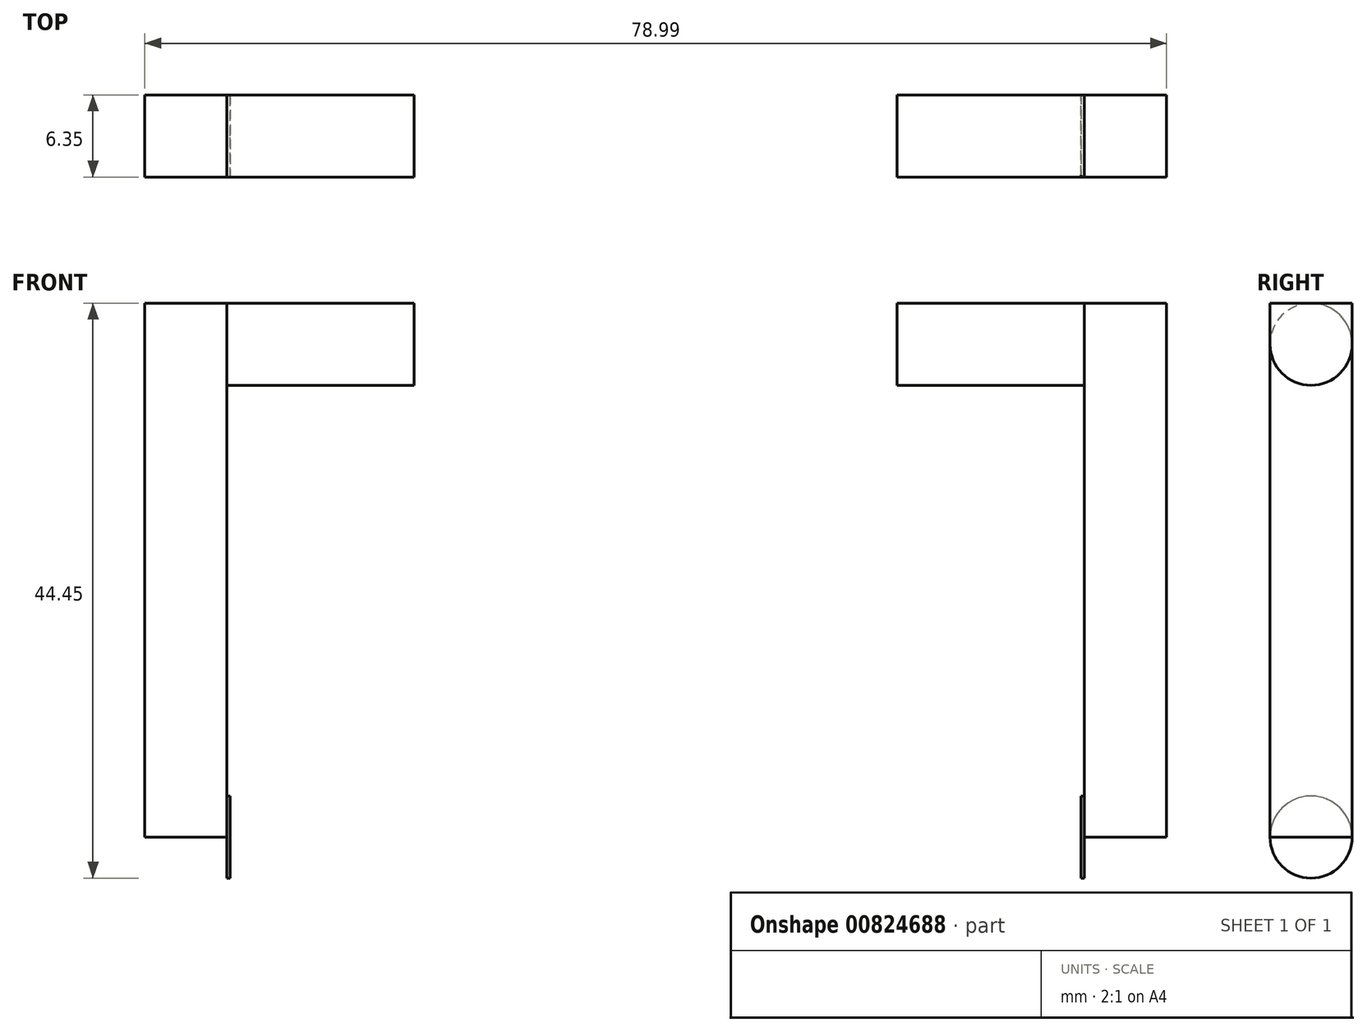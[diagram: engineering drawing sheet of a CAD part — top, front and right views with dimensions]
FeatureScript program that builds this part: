
annotation { "Feature Type Name" : "Feature", "Feature Type Description" : "" }
export const myFeature = defineFeature(function(context is Context, id is Id, definition is map)
    precondition{}
    {
        {
            var Q0;
            Q0=qCreatedBy(makeId("Front.planeOp"),FACE);
            var sketch = newSketch(context, id + "F0", { "sketchPlane" : qUnion([Q0])});
            skLineSegment(sketch, "E0.bottom", {"start": v(-26.92, 10.46) * mm, "end": v(-20.57, 10.46) * mm});
            skLineSegment(sketch, "E0.top", {"start": v(-26.92, -30.82) * mm, "end": v(-20.57, -30.82) * mm});
            skLineSegment(sketch, "E0.left", {"start": v(-26.92, 10.46) * mm, "end": v(-26.92, -30.82) * mm});
            skLineSegment(sketch, "E0.right", {"start": v(-20.57, 10.46) * mm, "end": v(-20.57, -30.82) * mm});
            skSolve(sketch);
        }
        {
            var Q0;
            Q0=qSketchRegion(id+"F0",true);
            extrude(context, id + "F1", {"entities" : qUnion([Q0]), "depth" : 6.35 * mm, "offsetDistance" : 25.4 * mm});
        }
        {
            var Q0;
            Q0=makeQuery(id+"F1.opExtrude","SWEPT_FACE",FACE,{"disambiguationData":[OSD([sQuery(id+"F0.wireOp",EDGE,"E0.right")])]});
            var sketch = newSketch(context, id + "F2", { "sketchPlane" : qUnion([Q0])});
            skLineSegment(sketch, "E1", {"start": v(-6.35, 10.46) * mm, "end": v(-6.35, 4.1) * mm});
            skLineSegment(sketch, "E2", {"start": v(-6.35, 4.1) * mm, "end": v(0, 4.1) * mm});
            skCircle(sketch, "E3", {"center": v(-3.18, 7.28) * mm, "radius": 3.17 * mm});
            skPoint(sketch, "E3.centerSnap0", {"position": v(-3.18, 10.46) * mm});
            skPoint(sketch, "E3.centerSnap1", {"position": v(-6.35, 7.28) * mm});
            skSolve(sketch);
        }
        {
            var Q0;
            {var subQ0=sQuery(id+"F2.wireOp",EDGE,"E3");var subQ4=makeQuery(id+"F2.imprint","INTERSECT",VERTEX,{"derivedFrom":[sQuery(id+"F2.wireOp",EDGE,"E1"),subQ0]});Q0=makeQuery(id+"F2.imprint","IMPRINT",FACE,{"disambiguationData":[TD([[makeQuery(id+"F2.imprint","IMPRINT",EDGE,{"disambiguationData":[TD([[subQ4,-1.0]])],"derivedFrom":subQ0}),1.0]])]});}
            extrude(context, id + "F3", {"entities" : qUnion([Q0]), "operationType" : NewBodyOperationType.ADD, "depth" : 14.48 * mm, "offsetDistance" : 25.4 * mm});
        }
        {
            var Q0;
            Q0=makeQuery(id+"F1.opExtrude","SWEPT_BODY",BODY,{"disambiguationData":[OSD([sQuery(id+"F0.wireOp",EDGE,"E0.bottom"),sQuery(id+"F0.wireOp",EDGE,"E0.top"),sQuery(id+"F0.wireOp",EDGE,"E0.left"),sQuery(id+"F0.wireOp",EDGE,"E0.right")])]});
            transform(context, id + "F4", {"entities" : qUnion([Q0]), "transformType" : TransformType.TRANSLATION_3D, "dx" : 79 * mm, "dy" : 0 * mm, "dz" : 0 * mm, "makeCopy" : true});
        }
        {
            var Q0;
            Q0=makeQuery(id+"F4.opPattern","COPY",FACE,{"derivedFrom":makeQuery(id+"F1.opExtrude","SWEPT_FACE",FACE,{"disambiguationData":[OSD([sQuery(id+"F0.wireOp",EDGE,"E0.left")])]}),"instanceName":"1"});
            var sketch = newSketch(context, id + "F5", { "sketchPlane" : qUnion([Q0])});
            skLineSegment(sketch, "E4", {"start": v(0, -30.82) * mm, "end": v(6.35, -30.82) * mm});
            skLineSegment(sketch, "E5", {"start": v(6.35, -30.82) * mm, "end": v(3.18, -30.82) * mm});
            skLineSegment(sketch, "E6", {"start": v(6.35, -30.82) * mm, "end": v(6.35, 10.46) * mm});
            skLineSegment(sketch, "E7", {"start": v(6.35, 10.46) * mm, "end": v(0, 10.46) * mm});
            skLineSegment(sketch, "E8", {"start": v(0, 10.46) * mm, "end": v(0, -30.82) * mm});
            skLineSegment(sketch, "E9", {"start": v(3.18, -30.82) * mm, "end": v(3.18, 10.46) * mm});
            skSolve(sketch);
        }
        {
            var Q0;
            Q0=sQuery(id+"F5.wireOp",EDGE,"E4");
            cPoint(context, id + "F6", {"entities" : qUnion([Q0]), "parameter" : 0.5});
        }
        {
            var Q0;
            Q0=makeQuery(id+"F4.opPattern","COPY",BODY,{"derivedFrom":makeQuery(id+"F1.opExtrude","SWEPT_BODY",BODY,{"disambiguationData":[OSD([sQuery(id+"F0.wireOp",EDGE,"E0.bottom"),sQuery(id+"F0.wireOp",EDGE,"E0.top"),sQuery(id+"F0.wireOp",EDGE,"E0.left"),sQuery(id+"F0.wireOp",EDGE,"E0.right")])]}),"instanceName":"1"});
            var Q1;
            Q1=qCreatedBy(id+"F6",VERTEX);
            var Q2;
            Q2=sQuery(id+"F5.wireOp",EDGE,"E9");
            transform(context, id + "F7", {"entities" : qUnion([Q0]), "transformType" : TransformType.ROTATION, "transformAxis" : qUnion([Q2]), "angle" : 180 * degree, "makeCopy" : false});
        }
        {
            var Q0;
            {var subQ0=sQuery(id+"F0.wireOp",EDGE,"E0.right");var subQ1=makeQuery(id+"F1.opExtrude","SWEPT_FACE",FACE,{"disambiguationData":[OSD([subQ0])]});var subQ2=sQuery(id+"F0.wireOp",EDGE,"E0.top");var subQ3=sQuery(id+"F0.wireOp",EDGE,"E0.left");var subQ4=sQuery(id+"F0.wireOp",EDGE,"E0.bottom");Q0=makeQuery(id+"F3.boolean.opBoolean","SPLIT",FACE,{"disambiguationData":[TD([makeQuery(id+"F1.opExtrude","CAP_FACE",FACE,{"disambiguationData":[OSD([subQ4,subQ2,subQ3,subQ0])],"isStart":true}),makeQuery(id+"F1.opExtrude","CAP_FACE",FACE,{"disambiguationData":[OSD([subQ4,subQ2,subQ3,subQ0])],"isStart":false}),makeQuery(id+"F1.opExtrude","SWEPT_FACE",FACE,{"disambiguationData":[OSD([subQ2])]}),subQ1,makeQuery(id+"F3.opExtrude","SWEPT_FACE",FACE,{"disambiguationData":[OSD([sQuery(id+"F2.wireOp",EDGE,"E3")])]})])],"derivedFrom":subQ1});}
            var sketch = newSketch(context, id + "F8", { "sketchPlane" : qUnion([Q0])});
            skLineSegment(sketch, "E10", {"start": v(-6.35, -30.82) * mm, "end": v(-6.35, -24.47) * mm});
            skLineSegment(sketch, "E11", {"start": v(-6.35, -24.47) * mm, "end": v(0, -24.47) * mm});
            skLineSegment(sketch, "E12", {"start": v(0, -24.47) * mm, "end": v(0, -30.82) * mm});
            skLineSegment(sketch, "E13", {"start": v(0, -30.82) * mm, "end": v(-6.35, -30.82) * mm});
            skPoint(sketch, "E14.centerSnap0", {"position": v(-3.18, -24.47) * mm});
            skPoint(sketch, "E14.centerSnap1", {"position": v(-6.35, -27.64) * mm});
            skLineSegment(sketch, "E15", {"start": v(-6.35, -30.82) * mm, "end": v(-6.35, -34) * mm});
            skLineSegment(sketch, "E16", {"start": v(-6.35, -34) * mm, "end": v(0, -34) * mm});
            skLineSegment(sketch, "E17", {"start": v(0, -34) * mm, "end": v(0, -30.82) * mm});
            skCircle(sketch, "E18", {"center": v(-3.18, -30.82) * mm, "radius": 3.17 * mm});
            skSolve(sketch);
        }
        {
            var Q0;
            {var subQ0=sQuery(id+"F8.wireOp",EDGE,"E13");Q0=makeQuery(id+"F8.imprint","IMPRINT",FACE,{"disambiguationData":[TD([[makeQuery(id+"F8.imprint","IMPRINT",EDGE,{"derivedFrom":subQ0}),-1.0]])]});}
            var Q1;
            {var subQ0=sQuery(id+"F8.wireOp",EDGE,"E13");Q1=makeQuery(id+"F8.imprint","IMPRINT",FACE,{"disambiguationData":[TD([[makeQuery(id+"F8.imprint","IMPRINT",EDGE,{"derivedFrom":subQ0}),1.0]])]});}
            extrude(context, id + "F9", {"entities" : qUnion([Q0, Q1]), "operationType" : NewBodyOperationType.ADD, "depth" : 0.25 * mm, "offsetDistance" : 25.4 * mm});
        }
        {
            var Q0;
            {var subQ0=sQuery(id+"F0.wireOp",EDGE,"E0.right");var subQ1=makeQuery(id+"F1.opExtrude","SWEPT_FACE",FACE,{"disambiguationData":[OSD([subQ0])]});var subQ2=sQuery(id+"F0.wireOp",EDGE,"E0.top");var subQ3=sQuery(id+"F0.wireOp",EDGE,"E0.left");var subQ4=sQuery(id+"F0.wireOp",EDGE,"E0.bottom");Q0=makeQuery(id+"F4.opPattern","COPY",FACE,{"derivedFrom":makeQuery(id+"F3.boolean.opBoolean","SPLIT",FACE,{"disambiguationData":[TD([makeQuery(id+"F1.opExtrude","CAP_FACE",FACE,{"disambiguationData":[OSD([subQ4,subQ2,subQ3,subQ0])],"isStart":true}),makeQuery(id+"F1.opExtrude","CAP_FACE",FACE,{"disambiguationData":[OSD([subQ4,subQ2,subQ3,subQ0])],"isStart":false}),makeQuery(id+"F1.opExtrude","SWEPT_FACE",FACE,{"disambiguationData":[OSD([subQ2])]}),subQ1,makeQuery(id+"F3.opExtrude","SWEPT_FACE",FACE,{"disambiguationData":[OSD([sQuery(id+"F2.wireOp",EDGE,"E3")])]})])],"derivedFrom":subQ1}),"instanceName":"1"});}
            var sketch = newSketch(context, id + "F10", { "sketchPlane" : qUnion([Q0])});
            skLineSegment(sketch, "E19", {"start": v(0, -30.82) * mm, "end": v(0, -24.47) * mm});
            skLineSegment(sketch, "E20", {"start": v(0, -24.47) * mm, "end": v(6.35, -24.47) * mm});
            skPoint(sketch, "E21.centerSnap0", {"position": v(3.18, -24.47) * mm});
            skPoint(sketch, "E21.centerSnap1", {"position": v(0, -27.64) * mm});
            skLineSegment(sketch, "E22", {"start": v(0, -30.82) * mm, "end": v(6.35, -30.82) * mm});
            skLineSegment(sketch, "E23", {"start": v(6.35, -30.82) * mm, "end": v(6.35, -34) * mm});
            skLineSegment(sketch, "E24", {"start": v(6.35, -34) * mm, "end": v(0, -34) * mm});
            skLineSegment(sketch, "E25", {"start": v(0, -34) * mm, "end": v(0, -30.82) * mm});
            skCircle(sketch, "E26", {"center": v(3.18, -30.82) * mm, "radius": 3.17 * mm});
            skSolve(sketch);
        }
        {
            var Q0;
            {var subQ0=sQuery(id+"F10.wireOp",EDGE,"E22");Q0=makeQuery(id+"F10.imprint","IMPRINT",FACE,{"disambiguationData":[TD([[makeQuery(id+"F10.imprint","IMPRINT",EDGE,{"derivedFrom":subQ0}),1.0]])]});}
            var Q1;
            {var subQ0=sQuery(id+"F10.wireOp",EDGE,"E22");Q1=makeQuery(id+"F10.imprint","IMPRINT",FACE,{"disambiguationData":[TD([[makeQuery(id+"F10.imprint","IMPRINT",EDGE,{"derivedFrom":subQ0}),-1.0]])]});}
            extrude(context, id + "F11", {"entities" : qUnion([Q0, Q1]), "operationType" : NewBodyOperationType.ADD, "depth" : 0.25 * mm, "offsetDistance" : 25.4 * mm});
        }
    });
